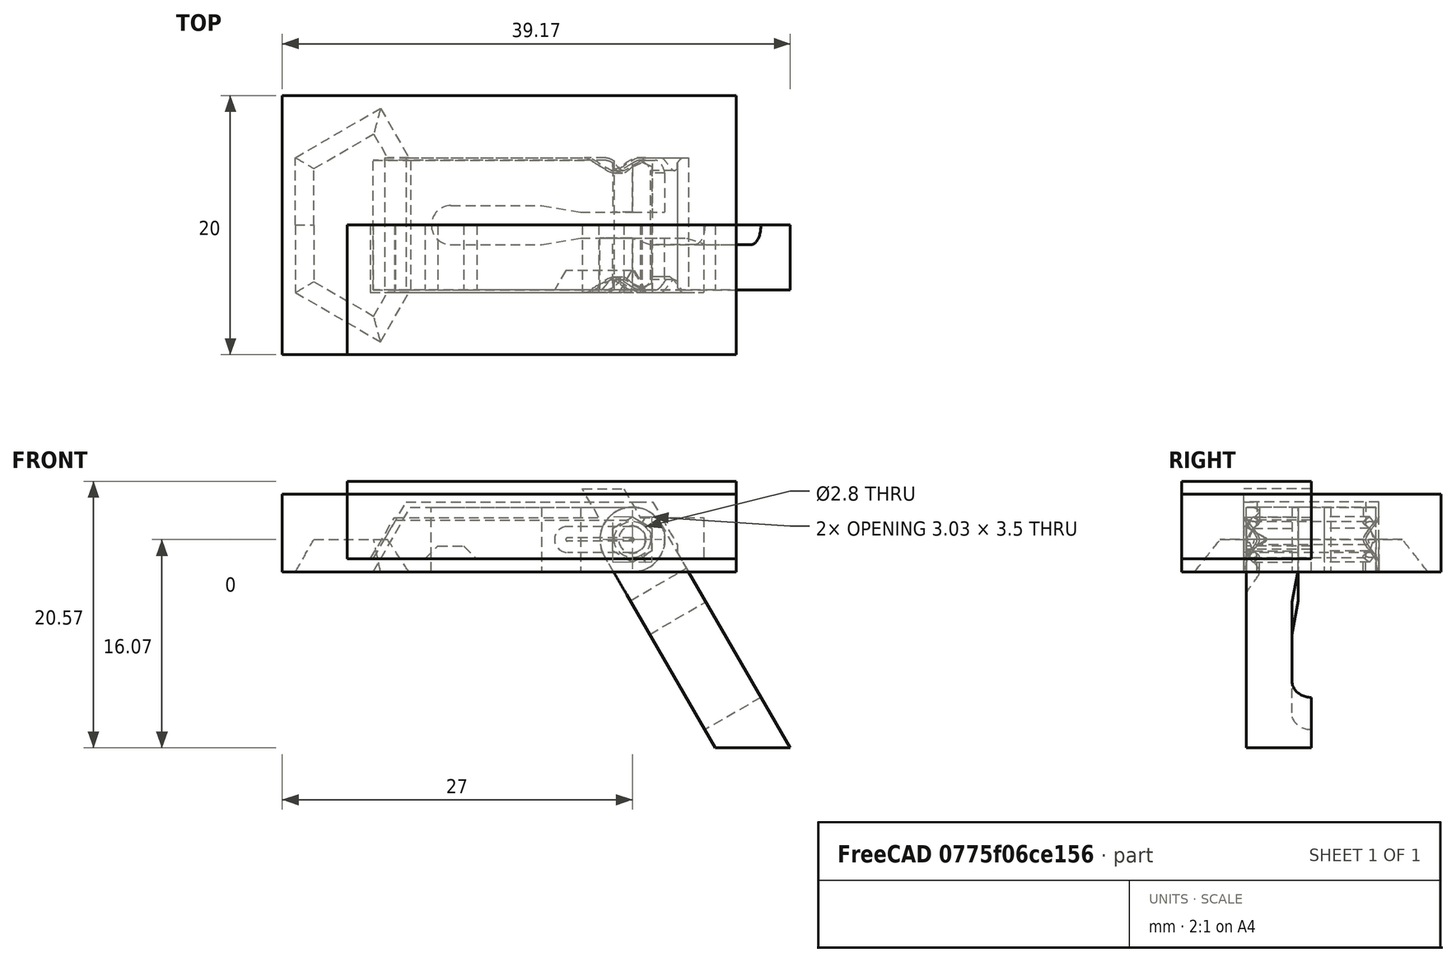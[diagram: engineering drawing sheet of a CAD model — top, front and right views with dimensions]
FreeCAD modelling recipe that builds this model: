
FCSTD DOCUMENT  (FreeCAD 1.0R38641 +1 (Git))
Label: feet2
License: All rights reserved
LicenseURL: https://en.wikipedia.org/wiki/All_rights_reserved
objects: Sketcher::SketchObject×13, PartDesign::Pad×8, PartDesign::Pocket×6, PartDesign::Body×5, Part::Mirroring×3, Part::MultiFuse×3, PartDesign::PolarPattern×2, Part::Cut×2, Part::Box×1, PartDesign::FeatureBase×1, PartDesign::SubShapeBinder×1, Part::Compound×1, Mesh::Feature×1
note: 90 computed .brp shape members not serialized (recipe doc carries the construction recipe); baked Part::Feature solids carry a one-line shape summary decoded from their .brp

FEATURE [Sketcher::SketchObject] Sketch003
  ArcFitTolerance = 1e-06
  AttachmentSupport = -> [XZ_Plane001]
  FullyConstrained = true
  MakeInternals = false
  MapMode = 5
  Placement = pos=(0,0,0) rot=(1,0,0;1.5708rad)
  sketch-geometry (13):
    g0: LineSegment StartX=-20 StartY=-1.5 StartZ=0 EndX=-18.2679 EndY=1.5 EndZ=0
    g1: LineSegment StartX=-18.2679 StartY=1.5 StartZ=0 EndX=0 EndY=1.5 EndZ=0
    g2: LineSegment StartX=-2e-16 StartY=-1.5 StartZ=0 EndX=-12 EndY=-1.5 EndZ=0
    g3: LineSegment StartX=-2e-16 StartY=-1.5 StartZ=0 EndX=0.75 EndY=-1.5 EndZ=0
    g4: LineSegment StartX=1.5 StartY=-0.75 StartZ=0 EndX=1.5 EndY=0 EndZ=0
    g5: ArcOfCircle CenterX=0 CenterY=0 CenterZ=0 NormalX=0 NormalY=0 NormalZ=1 AngleXU=0 Radius=1.5 StartAngle=0 EndAngle=1.5708
    g6: ArcOfCircle [constr] CenterX=0.75 CenterY=-0.75 CenterZ=0 NormalX=0 NormalY=0 NormalZ=1 AngleXU=0 Radius=0.75 StartAngle=4.71239 EndAngle=6.28319
    g7: GeomPoint [constr] X=1.5 Y=-1.5 Z=0
    g8: LineSegment StartX=0.75 StartY=-1.5 StartZ=0 EndX=1.5 EndY=-0.75 EndZ=0
    g9: LineSegment StartX=-16 StartY=-1.5 StartZ=0 EndX=-15 EndY=-0.5 EndZ=0
    g10: LineSegment StartX=-15 StartY=-0.5 StartZ=0 EndX=-13 EndY=-0.5 EndZ=0
    g11: LineSegment StartX=-13 StartY=-0.5 StartZ=0 EndX=-12 EndY=-1.5 EndZ=0
    g12: LineSegment StartX=-16 StartY=-1.5 StartZ=0 EndX=-20 EndY=-1.5 EndZ=0
  constraints (35):
    c: Coincident(g0,g1)
    c: Horizontal(g1)
    c: Coincident(g12,g0)
    c: Horizontal(g2)
    c: Symmetric(g2,g1,g-1)
    c: DistanceX(g12,g2) = 20
    c: DistanceY(g2,g1) = 3
    c: Angle(g2,g0) = 1.0472
    c: Coincident(g2,g3)
    c: Horizontal(g3)
    c: PointOnObject(g4,g-1)
    c: Vertical(g4)
    c: Coincident(g5,g-1)
    c: Coincident(g5,g4)
    c: Tangent(g5,g1) = 1.5708
    c: PointOnObject(g7,g3)
    c: PointOnObject(g7,g4)
    c: Tangent(g3,g6) = -1.5708
    c: Tangent(g4,g6) = -1.5708
    c: Coincident(g8,g3)
    c: Coincident(g8,g4)
    c: DistanceX(g3,g3) = 0.75
    c: PointOnObject(g9,g12)
    c: Coincident(g9,g10)
    c: Horizontal(g10)
    c: Coincident(g10,g11)
    c: DistanceY(g11,g10) = 1
    c: DistanceX(g10,g10) = 2
    c: Angle(g11,g2) = 0.785398
    c: Angle(g9,g2) = 2.35619
    c: DistanceX(g0,g9) = 4
    c: Coincident(g2,g11)
    c: PointOnObject(g12,g9)
    c: Horizontal(g12)
    c: Horizontal(g9,g2)
FEATURE [PartDesign::Pad] Pad001
  Direction = (0,-1,2e-16)
  Length = 5
  Length2 = 10
  Placement = pos=(0,0,0) rot=(1,0,0;1.5708rad)
  Profile = -> Sketch003
  ReferenceAxis = -> Sketch003 [N_Axis]
  Refine = true
  Suppressed = false
  Type = 0
FEATURE [Sketcher::SketchObject] Sketch004
  ArcFitTolerance = 1e-06
  AttachmentOffset = pos=(0,0,5) rot=(0,0,1;0rad)
  AttachmentSupport = -> [XZ_Plane001]
  FullyConstrained = true
  MakeInternals = false
  MapMode = 5
  Placement = pos=(0,-5,1.1e-15) rot=(1,0,0;1.5708rad)
  sketch-geometry (4):
    g0: ArcOfCircle CenterX=0 CenterY=0 CenterZ=0 NormalX=0 NormalY=0 NormalZ=1 AngleXU=0 Radius=1 StartAngle=4.71239 EndAngle=7.85398
    g1: ArcOfCircle CenterX=-5 CenterY=-2e-16 CenterZ=0 NormalX=0 NormalY=0 NormalZ=1 AngleXU=0 Radius=1 StartAngle=1.5708 EndAngle=4.71239
    g2: LineSegment StartX=-2e-16 StartY=-1 StartZ=0 EndX=-5 EndY=-1 EndZ=0
    g3: LineSegment StartX=3e-16 StartY=1 StartZ=0 EndX=-5 EndY=1 EndZ=0
  constraints (9):
    c: Tangent(g0,g2) = 1.5708
    c: Tangent(g0,g3) = -1.5708
    c: Tangent(g1,g2) = 1.5708
    c: Tangent(g1,g3) = -1.5708
    c: Equal(g0,g1)
    c: Horizontal(g3)
    c: Radius(g0) = 1
    c: Coincident(g0,g-1)
    c: DistanceX(g1,g0) = 5
FEATURE [PartDesign::Pocket] Pocket001
  BaseFeature = -> Pad001
  Direction = (0,1,-2e-16)
  Length = 1.5
  Length2 = 5
  Placement = pos=(0,0,0) rot=(1,0,0;1.5708rad)
  Profile = -> Sketch004
  ReferenceAxis = -> Sketch004 [N_Axis]
  Refine = true
  Suppressed = false
  TaperAngle = -30
  Type = 0
FEATURE [PartDesign::Body] Body001  label="A001"
  AllowCompound = false
  Group = -> [Sketch003,Pad001,Sketch004,Pocket001]
  Origin = -> Origin001
  Tip = -> Pocket001
FEATURE [Sketcher::SketchObject] Sketch005
  ArcFitTolerance = 1e-06
  AttachmentSupport = -> [XZ_Plane002]
  FullyConstrained = true
  MakeInternals = false
  MapMode = 5
  Placement = pos=(0,0,0) rot=(1,0,0;1.5708rad)
  sketch-geometry (14):
    g0: LineSegment StartX=-20.2 StartY=-1.5 StartZ=0 EndX=-18.3525 EndY=1.7 EndZ=0
    g1: LineSegment StartX=-18.3525 StartY=1.7 StartZ=0 EndX=-2.5815 EndY=1.7 EndZ=0
    g2: LineSegment StartX=-2.5815 StartY=1.7 StartZ=0 EndX=-3.85167 EndY=3.9 EndZ=0
    g3: LineSegment StartX=-3.85167 StartY=3.9 StartZ=0 EndX=-0.651666 EndY=3.9 EndZ=0
    g4: LineSegment StartX=-0.651666 StartY=3.9 StartZ=0 EndX=0.618505 EndY=1.7 EndZ=0
    g5: LineSegment StartX=0.618505 StartY=1.7 StartZ=0 EndX=5.5 EndY=1.7 EndZ=0
    g6: LineSegment StartX=5.5 StartY=1.7 StartZ=0 EndX=5.5 EndY=-1.5 EndZ=0
    g7: LineSegment StartX=5.5 StartY=-1.5 StartZ=0 EndX=8 EndY=-1.5 EndZ=0
    g8: LineSegment StartX=8 StartY=-1.5 StartZ=0 EndX=8 EndY=4.5 EndZ=0
    g9: LineSegment StartX=8 StartY=4.5 StartZ=0 EndX=-22 EndY=4.5 EndZ=0
    g10: LineSegment [constr] StartX=0 StartY=0 StartZ=0 EndX=-2.25167 EndY=3.9 EndZ=0
    g11: Circle [constr] CenterX=0 CenterY=0 CenterZ=0 NormalX=0 NormalY=0 NormalZ=1 AngleXU=0 Radius=1.80902
    g12: LineSegment StartX=-20.2 StartY=-1.5 StartZ=0 EndX=-22 EndY=-1.5 EndZ=0
    g13: LineSegment StartX=-22 StartY=-1.5 StartZ=0 EndX=-22 EndY=4.5 EndZ=0
  constraints (40):
    c: Coincident(g0,g1)
    c: Horizontal(g1)
    c: Coincident(g1,g2)
    c: Coincident(g2,g3)
    c: Horizontal(g3)
    c: Coincident(g3,g4)
    c: Coincident(g4,g5)
    c: Horizontal(g5)
    c: Coincident(g5,g6)
    c: Vertical(g6)
    c: Coincident(g6,g7)
    c: Horizontal(g7)
    c: Coincident(g7,g8)
    c: Vertical(g8)
    c: Coincident(g8,g9)
    c: Horizontal(g9)
    c: Parallel(g2,g4)
    c: Angle(g2,g1) = 1.0472
    c: DistanceX(g1,g4) = 3.2
    c: Horizontal(g4,g1)
    c: Horizontal(g6,g0)
    c: Angle(g0,g-1) = 2.0944
    c: DistanceY(g6) = -1.5
    c: DistanceY(g6,g6) = 3.2
    c: DistanceY(g8,g8) = 6
    c: Coincident(g10,g-1)
    c: Symmetric(g3,g3,g10)
    c: Parallel(g10,g4)
    c: DistanceX(g0) = -20.2
    c: Coincident(g11,g10)
    c: PointOnObject(g4,g11)
    c: DistanceY(g3,g8) = 0.6
    c: DistanceX(g5) = 5.5
    c: Coincident(g0,g12)
    c: Horizontal(g12)
    c: Coincident(g12,g13)
    c: Coincident(g13,g9)
    c: Vertical(g13)
    c: DistanceX(g9,g9) = 30
    c: DistanceX(g12) = -22
FEATURE [PartDesign::Pad] Pad002
  Direction = (0,-1,2e-16)
  Length = 5.2
  Length2 = 10
  Placement = pos=(0,0,0) rot=(1,0,0;1.5708rad)
  Profile = -> Sketch005
  ReferenceAxis = -> Sketch005 [N_Axis]
  Refine = true
  Suppressed = false
  Type = 0
FEATURE [Sketcher::SketchObject] Sketch006
  ArcFitTolerance = 1e-06
  AttachmentOffset = pos=(0,0,5.2) rot=(0,0,1;0rad)
  AttachmentSupport = -> [XZ_Plane002]
  FullyConstrained = true
  MakeInternals = false
  MapMode = 5
  Placement = pos=(0,-5.2,1.2e-15) rot=(1,0,0;1.5708rad)
  sketch-geometry (1):
    g0: Circle CenterX=0 CenterY=0 CenterZ=0 NormalX=0 NormalY=0 NormalZ=1 AngleXU=0 Radius=1.05
  constraints (2):
    c: Diameter(g0) = 2.1
    c: Coincident(g0,g-1)
FEATURE [PartDesign::Pad] Pad003
  BaseFeature = -> Pad002
  Direction = (0,-1,2e-16)
  Length = 1.6
  Length2 = 10
  Placement = pos=(0,0,0) rot=(1,0,0;1.5708rad)
  Profile = -> Sketch006
  ReferenceAxis = -> Sketch006 [N_Axis]
  Refine = true
  Reversed = true
  Suppressed = false
  TaperAngle = -30
  Type = 0
FEATURE [Sketcher::SketchObject] Sketch007
  ArcFitTolerance = 1e-06
  AttachmentOffset = pos=(0,0,5.2) rot=(0,0,1;0rad)
  AttachmentSupport = -> [XZ_Plane002]
  FullyConstrained = true
  MakeInternals = false
  MapMode = 5
  Placement = pos=(0,-5.2,1.2e-15) rot=(1,0,0;1.5708rad)
  sketch-geometry (4):
    g0: LineSegment StartX=-22 StartY=4.5 StartZ=0 EndX=-22 EndY=-1.5 EndZ=0
    g1: LineSegment StartX=-22 StartY=-1.5 StartZ=0 EndX=8 EndY=-1.5 EndZ=0
    g2: LineSegment StartX=8 StartY=-1.5 StartZ=0 EndX=8 EndY=4.5 EndZ=0
    g3: LineSegment StartX=8 StartY=4.5 StartZ=0 EndX=-22 EndY=4.5 EndZ=0
  constraints (12):
    c: Coincident(g0,g1)
    c: Coincident(g1,g2)
    c: Coincident(g2,g3)
    c: Coincident(g3,g0)
    c: Vertical(g0)
    c: Vertical(g2)
    c: Horizontal(g1)
    c: Horizontal(g3)
    c: DistanceX(g3,g3) = 30
    c: DistanceY(g0,g0) = 6
    c: DistanceX(g0) = -22
    c: DistanceY(g1) = -1.5
FEATURE [PartDesign::Pad] Pad004
  BaseFeature = -> Pad003
  Direction = (0,-1,2e-16)
  Length = 4.8
  Length2 = 10
  Placement = pos=(0,0,0) rot=(1,0,0;1.5708rad)
  Profile = -> Sketch007
  ReferenceAxis = -> Sketch007 [N_Axis]
  Refine = true
  Suppressed = false
  Type = 0
FEATURE [PartDesign::Body] Body002  label="A002"
  AllowCompound = true
  Group = -> [Sketch005,Pad002,Sketch006,Pad003,Sketch007,Pad004]
  Origin = -> Origin002
  Tip = -> Pad004
FEATURE [Sketcher::SketchObject] Sketch008
  ArcFitTolerance = 1e-06
  AttachmentSupport = -> [XZ_Plane003]
  FullyConstrained = true
  MakeInternals = false
  MapMode = 5
  Placement = pos=(0,0,0) rot=(1,0,0;1.5708rad)
  sketch-geometry (4):
    g0: LineSegment StartX=-20 StartY=-2.5 StartZ=0 EndX=-17.1132 EndY=2.5 EndZ=0
    g1: LineSegment StartX=-17.1132 StartY=2.5 StartZ=0 EndX=0 EndY=2.5 EndZ=0
    g2: LineSegment StartX=-5e-16 StartY=-2.5 StartZ=0 EndX=-20 EndY=-2.5 EndZ=0
    g3: ArcOfCircle CenterX=0 CenterY=0 CenterZ=0 NormalX=0 NormalY=0 NormalZ=1 AngleXU=0 Radius=2.5 StartAngle=4.71239 EndAngle=7.85398
  constraints (11):
    c: Coincident(g0,g1)
    c: Horizontal(g1)
    c: Horizontal(g2)
    c: DistanceX(g0,g2) = 20
    c: Angle(g2,g0) = 1.0472
    c: PointOnObject(g2,g-2)
    c: Coincident(g2,g0)
    c: Coincident(g3,g-1)
    c: Tangent(g3,g1) = 1.5708
    c: Coincident(g3,g2)
    c: Radius(g3) = 2.5
FEATURE [PartDesign::Pad] Pad005
  Direction = (0,-1,2e-16)
  Length = 5
  Length2 = 10
  Placement = pos=(0,0,0) rot=(1,0,0;1.5708rad)
  Profile = -> Sketch008
  ReferenceAxis = -> Sketch008 [N_Axis]
  Refine = true
  Suppressed = false
  Type = 0
FEATURE [Sketcher::SketchObject] Sketch009
  ArcFitTolerance = 1e-06
  AttachmentOffset = pos=(0,0,5) rot=(0,0,1;0rad)
  AttachmentSupport = -> [XZ_Plane003]
  FullyConstrained = true
  MakeInternals = false
  MapMode = 5
  Placement = pos=(0,-5,1.1e-15) rot=(1,0,0;1.5708rad)
  sketch-geometry (7):
    g0: LineSegment StartX=1.51554 StartY=-0.875 StartZ=0 EndX=1.51554 EndY=0.875 EndZ=0
    g1: LineSegment StartX=1.51554 StartY=0.875 StartZ=0 EndX=-2e-16 EndY=1.75 EndZ=0
    g2: LineSegment StartX=-2e-16 StartY=1.75 StartZ=0 EndX=-1.51554 EndY=0.875 EndZ=0
    g3: LineSegment StartX=-1.51554 StartY=0.875 StartZ=0 EndX=-1.51554 EndY=-0.875 EndZ=0
    g4: LineSegment StartX=-1.51554 StartY=-0.875 StartZ=0 EndX=0 EndY=-1.75 EndZ=0
    g5: LineSegment StartX=0 StartY=-1.75 StartZ=0 EndX=1.51554 EndY=-0.875 EndZ=0
    g6: Circle [constr] CenterX=0 CenterY=0 CenterZ=0 NormalX=0 NormalY=0 NormalZ=1 AngleXU=0 Radius=1.75
  constraints (17):
    c: Coincident(g0,g1)
    c: Coincident(g1,g2)
    c: Coincident(g2,g3)
    c: Coincident(g3,g4)
    c: Coincident(g4,g5)
    c: Coincident(g5,g0)
    c: Equal(g0, g1-g5) x5
    c: PointOnObject(g0,g6)
    c: PointOnObject(g1,g6)
    c: PointOnObject(g2,g6)
    c: PointOnObject(g3,g6)
    c: PointOnObject(g4,g6)
    c: PointOnObject(g5,g6)
    c: Coincident(g6,g-1)
    c: Diameter(g6) = 3.5
    c: Vertical(g3)
    c: DistanceX(g3,g0) = 3.03109
FEATURE [PartDesign::Pocket] Pocket002
  BaseFeature = -> Pad005
  Direction = (0,1,-2e-16)
  Length = 1.5
  Length2 = 5
  Placement = pos=(0,0,0) rot=(1,0,0;1.5708rad)
  Profile = -> Sketch009
  ReferenceAxis = -> Sketch009 [N_Axis]
  Refine = true
  Suppressed = false
  Type = 1
FEATURE [Sketcher::SketchObject] Sketch010
  ArcFitTolerance = 1e-06
  AttachmentSupport = -> [XZ_Plane004]
  FullyConstrained = true
  MakeInternals = false
  MapMode = 5
  Placement = pos=(0,0,0) rot=(1,0,0;1.5708rad)
  sketch-geometry (17):
    g0: LineSegment StartX=8 StartY=-2.5 StartZ=0 EndX=8 EndY=3.5 EndZ=0
    g1: LineSegment StartX=8 StartY=3.5 StartZ=0 EndX=-27 EndY=3.5 EndZ=0
    g2: LineSegment StartX=-27 StartY=3.5 StartZ=0 EndX=-27 EndY=-2.5 EndZ=0
    g3: LineSegment StartX=-27 StartY=-2.5 StartZ=0 EndX=-21.5588 EndY=-2.5 EndZ=0
    g4: LineSegment StartX=-21.5588 StartY=-2.5 StartZ=0 EndX=-20.1155 EndY=0 EndZ=0
    g5: LineSegment StartX=-20.1155 StartY=0 StartZ=0 EndX=-19.1155 EndY=0 EndZ=0
    g6: LineSegment StartX=-19.1155 StartY=0 StartZ=0 EndX=-17.4412 EndY=2.9 EndZ=0
    g7: LineSegment StartX=-17.4412 StartY=2.9 StartZ=0 EndX=1.55885 EndY=2.9 EndZ=0
    g8: LineSegment StartX=4.67654 StartY=-2.5 StartZ=0 EndX=8 EndY=-2.5 EndZ=0
    g9: LineSegment [constr] StartX=4.67654 StartY=-2.5 StartZ=0 EndX=0 EndY=-2.5 EndZ=0
    g10: LineSegment [constr] StartX=1.21244 StartY=2.9 StartZ=0 EndX=4.33013 EndY=-2.5 EndZ=0
    g11: LineSegment StartX=1.55885 StartY=2.9 StartZ=0 EndX=3.4641 EndY=-0.4 EndZ=0
    g12: LineSegment [constr] StartX=3.4641 StartY=-0.4 StartZ=0 EndX=4.67654 EndY=-2.5 EndZ=0
    g13: LineSegment StartX=3.4641 StartY=-0.4 StartZ=0 EndX=3.4641 EndY=-1 EndZ=0
    g14: LineSegment StartX=3.4641 StartY=-1 StartZ=0 EndX=4.33013 EndY=-2.5 EndZ=0
    g15: LineSegment StartX=4.33013 StartY=-2.5 StartZ=0 EndX=4.67654 EndY=-2.5 EndZ=0
    g16: Circle CenterX=0 CenterY=0 CenterZ=0 NormalX=0 NormalY=0 NormalZ=1 AngleXU=0 Radius=1.4
  constraints (50):
    c: Coincident(g0,g1)
    c: Coincident(g1,g2)
    c: Horizontal(g1)
    c: Vertical(g0)
    c: Vertical(g2)
    c: DistanceY(g0) = -2.5
    c: DistanceY(g0,g0) = 6
    c: Coincident(g2,g3)
    c: Horizontal(g3)
    c: Coincident(g3,g4)
    c: PointOnObject(g4,g-1)
    c: Coincident(g4,g5)
    c: PointOnObject(g5,g-1)
    c: Coincident(g5,g6)
    c: Coincident(g6,g7)
    c: Horizontal(g7)
    c: Coincident(g7,g11)
    c: DistanceY(g7) = 2.9
    c: Coincident(g8,g12)
    c: Coincident(g8,g0)
    c: Horizontal(g8)
    c: Angle(g6,g7) = 2.0944
    c: Horizontal(g3,g12)
    c: DistanceX(g7,g7) = 19
    c: DistanceX(g5,g5) = 1
    c: DistanceX(g1,g1) = 35
    c: DistanceX(g0) = 8
    c: DistanceY(g7,g0) = 0.6
    c: Coincident(g9,g12)
    c: Horizontal(g9)
    c: PointOnObject(g10,g7)
    c: PointOnObject(g10,g9)
    c: Coincident(g11,g12)
    c: Parallel(g10,g11)
    c: Parallel(g10,g12)
    c: Coincident(g13,g11)
    c: PointOnObject(g13,g10)
    c: Coincident(g14,g13)
    c: Coincident(g14,g10)
    c: Coincident(g15,g10)
    c: Coincident(g15,g8)
    c: Vertical(g13)
    c: Angle(g7,g11) = 2.0944
    c: DistanceY(g13) = -1
    c: Parallel(g4,g6)
    c: PointOnObject(g9,g-2)
    c: Distance(g-1,g10) = 2.5
    c: Distance(g-1,g11) = 2.8
    c: Coincident(g16,g-1)
    c: Diameter(g16) = 2.8
FEATURE [PartDesign::Pad] Pad006
  Direction = (0,-1,2e-16)
  Length = 5.2
  Length2 = 10
  Placement = pos=(0,0,0) rot=(1,0,0;1.5708rad)
  Profile = -> Sketch010
  ReferenceAxis = -> Sketch010 [N_Axis]
  Refine = true
  Suppressed = false
  Type = 0
FEATURE [Sketcher::SketchObject] Sketch012
  ArcFitTolerance = 1e-06
  AttachmentOffset = pos=(0,0,5.2) rot=(0,0,1;0rad)
  AttachmentSupport = -> [XZ_Plane004]
  FullyConstrained = true
  MakeInternals = false
  MapMode = 5
  Placement = pos=(0,-5.2,1.2e-15) rot=(1,0,0;1.5708rad)
  sketch-geometry (4):
    g0: LineSegment StartX=-27 StartY=3.5 StartZ=0 EndX=-27 EndY=-2.5 EndZ=0
    g1: LineSegment StartX=-27 StartY=-2.5 StartZ=0 EndX=8 EndY=-2.5 EndZ=0
    g2: LineSegment StartX=8 StartY=-2.5 StartZ=0 EndX=8 EndY=3.5 EndZ=0
    g3: LineSegment StartX=8 StartY=3.5 StartZ=0 EndX=-27 EndY=3.5 EndZ=0
  constraints (12):
    c: Coincident(g0,g1)
    c: Coincident(g1,g2)
    c: Coincident(g2,g3)
    c: Coincident(g3,g0)
    c: Vertical(g0)
    c: Vertical(g2)
    c: Horizontal(g1)
    c: Horizontal(g3)
    c: DistanceX(g3,g3) = 35
    c: DistanceY(g0,g0) = 6
    c: DistanceY(g1) = -2.5
    c: DistanceX(g2) = 8
FEATURE [Part::Box] Box  label="Cube"
  AttacherType = Attacher::AttachEngine3D
  Height = 6
  Length = 35
  Placement = pos=(-27,-10,-2.5) rot=(0,0,1;0rad)
  Width = 10
FEATURE [Sketcher::SketchObject] Sketch016
  ArcFitTolerance = 1e-06
  AttachmentSupport = -> [XY_Plane003]
  FullyConstrained = true
  MakeInternals = false
  MapMode = 5
  sketch-geometry (8):
    g0: ArcOfCircle CenterX=-14 CenterY=0 CenterZ=0 NormalX=0 NormalY=0 NormalZ=1 AngleXU=0 Radius=1.5 StartAngle=1.5708 EndAngle=4.71239
    g1: LineSegment StartX=4 StartY=1 StartZ=0 EndX=4 EndY=-1 EndZ=0
    g2: LineSegment StartX=-4 StartY=1 StartZ=0 EndX=4 EndY=1 EndZ=0
    g3: LineSegment StartX=-14 StartY=1.5 StartZ=0 EndX=-7 EndY=1.5 EndZ=0
    g4: LineSegment StartX=-7 StartY=1.5 StartZ=0 EndX=-4 EndY=1 EndZ=0
    g5: LineSegment StartX=-14 StartY=-1.5 StartZ=0 EndX=-7 EndY=-1.5 EndZ=0
    g6: LineSegment StartX=-7 StartY=-1.5 StartZ=0 EndX=-4 EndY=-1 EndZ=0
    g7: LineSegment StartX=-4 StartY=-1 StartZ=0 EndX=4 EndY=-1 EndZ=0
  constraints (25):
    c: DistanceY(g7) = -1
    c: DistanceX(g5) = -14
    c: Coincident(g5,g0) = -1.5708
    c: Coincident(g0,g3) = 1.5708
    c: Coincident(g2,g1)
    c: Coincident(g1,g7)
    c: Vertical(g1)
    c: PointOnObject(g0,g-1)
    c: DistanceX(g7) = 4
    c: Coincident(g4,g2)
    c: Horizontal(g2)
    c: Coincident(g3,g4)
    c: Horizontal(g3)
    c: Coincident(g5,g6)
    c: Horizontal(g5)
    c: Coincident(g6,g7)
    c: Horizontal(g7)
    c: Radius(g0) = 1.5
    c: Vertical(g5,g3)
    c: DistanceX(g6,g6) = 3
    c: Equal(g4,g6)
    c: Equal(g3,g5)
    c: Vertical(g0,g0)
    c: DistanceX(g2) = -4
    c: Vertical(g2,g6)
FEATURE [Sketcher::SketchObject] Sketch
  ArcFitTolerance = 1e-06
  AttachmentOffset = pos=(0,0,0) rot=(0,0,1;-1.5708rad)
  AttachmentSupport = -> [YZ_Plane003]
  FullyConstrained = false
  MakeInternals = false
  MapMode = 5
  Placement = pos=(0,0,0) rot=(0,-1,0;4.71239rad)
  sketch-geometry (18):
    g0-g3: Circle [constr] x4 (B-spline internal-alignment scaffolding for g4; pole/knot coordinates omitted)
    g4: BSplineCurve PolesCount=6 KnotsCount=3 Degree=3 IsPeriodic=0
    g5: GeomPoint [constr] X=1.75 Y=-5 Z=0
    g6: GeomPoint [constr] X=0 Y=-4 Z=0
    g7: GeomPoint [constr] X=-1.75 Y=-5 Z=0
    g8: Circle [constr] CenterX=0.442329 CenterY=-4 CenterZ=0 NormalX=0 NormalY=0 NormalZ=1 AngleXU=0 Radius=1
    g9: Circle [constr] CenterX=-0.442329 CenterY=-4 CenterZ=0 NormalX=0 NormalY=0 NormalZ=1 AngleXU=0 Radius=1
    g10: LineSegment [constr] StartX=-1.75 StartY=-5 StartZ=0 EndX=-1.30767 EndY=-5 EndZ=0
    g11: LineSegment [constr] StartX=1.30767 StartY=-5 StartZ=0 EndX=1.75 EndY=-5 EndZ=0
    g12: LineSegment [constr] StartX=0.442329 StartY=-4 StartZ=0 EndX=1.30767 EndY=-5 EndZ=0
    g13: LineSegment [constr] StartX=-0.442329 StartY=-4 StartZ=0 EndX=0 EndY=-4 EndZ=0
    g14: LineSegment [constr] StartX=0.442329 StartY=-4 StartZ=0 EndX=0 EndY=-4 EndZ=0
    g15: LineSegment StartX=-1.75 StartY=-5 StartZ=0 EndX=-1.75 EndY=-7.07699 EndZ=0
    g16: LineSegment StartX=-1.75 StartY=-7.07699 StartZ=0 EndX=1.75 EndY=-7.07699 EndZ=0
    g17: LineSegment StartX=1.75 StartY=-7.07699 StartZ=0 EndX=1.75 EndY=-5 EndZ=0
  constraints (40):
    c: Weight(g0) = 1
    c: Equal(g0,g1)
    c: Equal(g0,g2)
    c: Equal(g0,g3)
    c: InternalAlignment(g0-g3 -> g4) x4
    c: InternalAlignment(g5,g4)
    c: InternalAlignment(g6,g4)
    c: InternalAlignment(g7,g4)
    c: Horizontal(g2,g4)
    c: Horizontal(g4,g1)
    c: Horizontal(g1,g4)
    c: PointOnObject(g6,g-2)
    c: DistanceY(g4) = -5
    c: InternalAlignment(g8,g4)
    c: Equal(g8,g0)
    c: InternalAlignment(g9,g4)
    c: Equal(g9,g0)
    c: Horizontal(g8,g9)
    c: Coincident(g10,g4)
    c: Coincident(g10,g2)
    c: Coincident(g11,g1)
    c: Coincident(g11,g4)
    c: Coincident(g12,g8)
    c: Coincident(g12,g1)
    c: Coincident(g13,g9)
    c: Coincident(g13,g6)
    c: Coincident(g14,g8)
    c: Coincident(g14,g6)
    c: Equal(g14,g11)
    c: Equal(g13,g10)
    c: DistanceX(g4) = 1.75
    c: DistanceX(g4) = -1.75
    c: DistanceY(g6) = -4
    c: Coincident(g15,g4)
    c: Vertical(g15)
    c: Coincident(g15,g16)
    c: Horizontal(g16)
    c: Coincident(g16,g17)
    c: Coincident(g17,g4)
    c: Vertical(g17)
FEATURE [PartDesign::Pocket] Pocket004
  BaseFeature = -> Pocket002
  Direction = (-1,0,0)
  Length = 5
  Length2 = 5
  Placement = pos=(0,0,0) rot=(1,0,0;1.5708rad)
  Profile = -> Sketch
  ReferenceAxis = -> Sketch [N_Axis]
  Refine = true
  Reversed = true
  Suppressed = false
  Type = 0
FEATURE [PartDesign::PolarPattern] PolarPattern001
  Angle = 360
  Axis = -> Y_Axis003
  BaseFeature = -> Pocket002
  Mode = 1
  Occurrences = 4
  Offset = 120
  Originals = -> [Pocket004]
  Placement = pos=(0,0,0) rot=(1,0,0;1.5708rad)
  Refine = true
  Suppressed = false
  TransformMode = 0
FEATURE [PartDesign::Pocket] Pocket005
  BaseFeature = -> PolarPattern001
  Direction = (0,0,-1)
  Length = 5
  Length2 = 5
  Midplane = true
  Placement = pos=(0,0,0) rot=(1,0,0;1.5708rad)
  Profile = -> Sketch016
  ReferenceAxis = -> Sketch016 [N_Axis]
  Refine = true
  Suppressed = false
  Type = 1
FEATURE [PartDesign::Body] Body003  label="B001"
  AllowCompound = false
  Group = -> [Sketch008,Pad005,Sketch009,Pocket002,Pocket004,Sketch016,PolarPattern001,Sketch,Pocket005]
  Origin = -> Origin003
  Tip = -> Pocket005
FEATURE [PartDesign::FeatureBase] Clone
  BaseFeature = -> Body003
  Suppressed = false
FEATURE [PartDesign::Body] Body005
  AllowCompound = false
  Group = -> [Clone]
  Origin = -> Origin005
  Placement = pos=(0,0,0) rot=(0,1,0;4.18879rad)
  Tip = -> Clone
FEATURE [Part::Cut] Cut
  Base = -> Box
  Refine = true
  Tool = -> Body003
FEATURE [Part::Mirroring] Part__Mirroring001  label="B001 (Mirror #2)"
  Base = (0,0,0)
  Normal = (0,1,0)
  Source = -> Body003
FEATURE [Part::MultiFuse] Fusion001
  Refine = true
  Shapes = -> [Body003,Part__Mirroring001]
FEATURE [PartDesign::SubShapeBinder] Binder
  BindCopyOnChange = 0
  BindMode = 0
  ClaimChildren = false
  Context = -> Body004 [Binder.]
  Fuse = false
  MakeFace = true
  OffsetFill = false
  OffsetIntersection = false
  OffsetJoinType = 0
  OffsetOpenResult = false
  PartialLoad = false
  Placement = pos=(0,-0.2,0) rot=(0,0,1;0rad)
  Refine = true
  Relative = true
  Support = -> [Body003[Sketch.]]
  _Version = 2
FEATURE [PartDesign::Pad] Pad
  BaseFeature = -> Pad006
  Direction = (1,0,0)
  Length = 6
  Length2 = 10
  Placement = pos=(0,0,0) rot=(1,0,0;1.5708rad)
  Profile = -> Binder
  Refine = true
  Suppressed = false
  Type = 0
FEATURE [PartDesign::PolarPattern] PolarPattern002
  Angle = 360
  Axis = -> Y_Axis004
  BaseFeature = -> Pad
  Mode = 0
  Occurrences = 3
  Offset = 120
  Originals = -> [Pad]
  Placement = pos=(0,0,0) rot=(1,0,0;1.5708rad)
  Refine = true
  Suppressed = false
  TransformMode = 0
FEATURE [PartDesign::Pad] Pad008
  BaseFeature = -> PolarPattern002
  Direction = (0,-1,2e-16)
  Length = 4.8
  Length2 = 10
  Placement = pos=(0,0,0) rot=(1,0,0;1.5708rad)
  Profile = -> Sketch012
  ReferenceAxis = -> Sketch012 [N_Axis]
  Refine = true
  Suppressed = false
  Type = 0
FEATURE [Sketcher::SketchObject] Sketch017
  ArcFitTolerance = 1e-06
  AttachmentSupport = -> [XZ_Plane004]
  FullyConstrained = false
  MakeInternals = false
  MapMode = 5
  Placement = pos=(0,0,0) rot=(1,0,0;1.5708rad)
  sketch-geometry (8):
    g0: LineSegment StartX=-27 StartY=3.5 StartZ=0 EndX=-27 EndY=-2.5 EndZ=0
    g1: LineSegment StartX=-27 StartY=-2.5 StartZ=0 EndX=8 EndY=-2.5 EndZ=0
    g2: LineSegment StartX=8 StartY=-2.5 StartZ=0 EndX=8 EndY=3.5 EndZ=0
    g3: LineSegment StartX=8 StartY=3.5 StartZ=0 EndX=-27 EndY=3.5 EndZ=0
    g4: LineSegment StartX=-82.4426 StartY=43.1102 StartZ=0 EndX=-82.4426 EndY=-32.4768 EndZ=0
    g5: LineSegment StartX=-82.4426 StartY=-32.4768 StartZ=0 EndX=65.6399 EndY=-32.4768 EndZ=0
    g6: LineSegment StartX=65.6399 StartY=-32.4768 StartZ=0 EndX=65.6399 EndY=43.1102 EndZ=0
    g7: LineSegment StartX=65.6399 StartY=43.1102 StartZ=0 EndX=-82.4426 EndY=43.1102 EndZ=0
  constraints (20):
    c: Coincident(g0,g1)
    c: Coincident(g1,g2)
    c: Coincident(g2,g3)
    c: Coincident(g3,g0)
    c: Vertical(g2)
    c: Horizontal(g1)
    c: Horizontal(g3)
    c: Distance(g0,g2) = 35
    c: Distance(g1,g3) = 6
    c: DistanceY(g0) = -2.5
    c: DistanceX(g2) = 8
    c: Vertical(g0)
    c: Coincident(g4,g5)
    c: Coincident(g5,g6)
    c: Coincident(g6,g7)
    c: Coincident(g7,g4)
    c: Vertical(g4)
    c: Vertical(g6)
    c: Horizontal(g5)
    c: Horizontal(g7)
FEATURE [PartDesign::Pocket] Pocket
  BaseFeature = -> Pad008
  Direction = (0,1,-2e-16)
  Length = 5
  Length2 = 5
  Midplane = true
  Placement = pos=(0,0,0) rot=(1,0,0;1.5708rad)
  Profile = -> Sketch017
  ReferenceAxis = -> Sketch017 [N_Axis]
  Refine = true
  Suppressed = false
  Type = 1
FEATURE [Sketcher::SketchObject] Sketch018
  ArcFitTolerance = 1e-06
  AttachmentSupport = -> [Pocket]
  FullyConstrained = true
  MakeInternals = false
  MapMode = 5
  Placement = pos=(0,-1.1e-15,-2.5) rot=(1,0,0;3.14159rad)
  sketch-geometry (5):
    g0: LineSegment StartX=-26 StartY=-5 StartZ=0 EndX=-26 EndY=5.2 EndZ=0
    g1: LineSegment StartX=-26 StartY=5.2 StartZ=0 EndX=-19.4182 EndY=9 EndZ=0
    g2: LineSegment StartX=-19.4182 StartY=9 StartZ=0 EndX=-17.2243 EndY=5.2 EndZ=0
    g3: LineSegment StartX=-17.2243 StartY=5.2 StartZ=0 EndX=-17.2243 EndY=-5 EndZ=0
    g4: LineSegment StartX=-17.2243 StartY=-5 StartZ=0 EndX=-26 EndY=-5 EndZ=0
  constraints (15):
    c: Coincident(g1,g2)
    c: Coincident(g2,g3)
    c: Vertical(g3)
    c: Coincident(g3,g4)
    c: Horizontal(g4)
    c: Angle(g0,g1) = 2.0944
    c: Perpendicular(g1,g2)
    c: DistanceY(g1) = 9
    c: Equal(g3,g0)
    c: Coincident(g1,g0)
    c: Vertical(g0)
    c: Coincident(g0,g4)
    c: DistanceX(g0) = -26
    c: DistanceY(g0) = 5.2
    c: DistanceY(g0) = -5
FEATURE [PartDesign::Pocket] Pocket006
  BaseFeature = -> Pocket
  Direction = (0,0,1)
  Length = 2.5
  Length2 = 5
  Placement = pos=(0,0,0) rot=(1,0,0;1.5708rad)
  Profile = -> Sketch018
  ReferenceAxis = -> Sketch018 [N_Axis]
  Refine = true
  Suppressed = false
  TaperAngle = -30
  Type = 0
FEATURE [PartDesign::Body] Body004  label="B002"
  AllowCompound = true
  Group = -> [Sketch010,Pad006,Sketch012,Binder,Pad,PolarPattern002,Sketch017,Pad008,Pocket,Sketch018,Pocket006]
  Origin = -> Origin004
  Tip = -> Pocket006
FEATURE [Part::Cut] Cut001
  Base = -> Cut
  Refine = true
  Tool = -> Body004
FEATURE [Part::Mirroring] Part__Mirroring  label="Cut001 (Mirror #1)"
  Base = (-26,-2e-16,-2.5)
  MirrorPlane = -> Cut001 [Face1]
  Normal = (0,1,0)
  Source = -> Cut001
FEATURE [Part::MultiFuse] Fusion
  Refine = true
  Shapes = -> [Cut001,Part__Mirroring]
FEATURE [Part::Mirroring] Part__Mirroring002  label="B002 (Mirror #3)"
  Base = (0,0,0)
  Normal = (0,1,0)
  Source = -> Body004
FEATURE [Part::MultiFuse] Fusion002
  Refine = true
  Shapes = -> [Body004,Part__Mirroring002]
FEATURE [Part::Compound] Compound
  Links = -> [Fusion001,Fusion002]
FEATURE [Mesh::Feature] Mesh  label="Compound (Meshed)"
